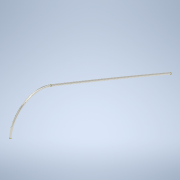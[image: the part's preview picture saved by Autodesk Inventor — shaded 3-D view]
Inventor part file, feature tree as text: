
AUTODESK INVENTOR PART (.ipt)
format: ipt  version: 2022 (Build 260153000, 153)  size: 117,760 bytes
history: native  units: in
note: dims shown in document units (in); Inventor stores cm internally (conversion verified against a paired STEP export)
features: sketch x2, sweep x1
ambient origin geometry x8: Origin, YZ Plane, XZ Plane, XY Plane, X Axis, Y Axis, Z Axis, Center Point
bodies: Solid1 (feature_tree)
feature tree (3):
  sweep  "Sweep1"
  sketch  "Sketch3"  dims[d10=0.001in d11=0.0059in]
  sketch  "Sketch4"  dims[d12=0.013in d13=0.0807in d14=90.0deg d15=0.0in d16=0.0in]
